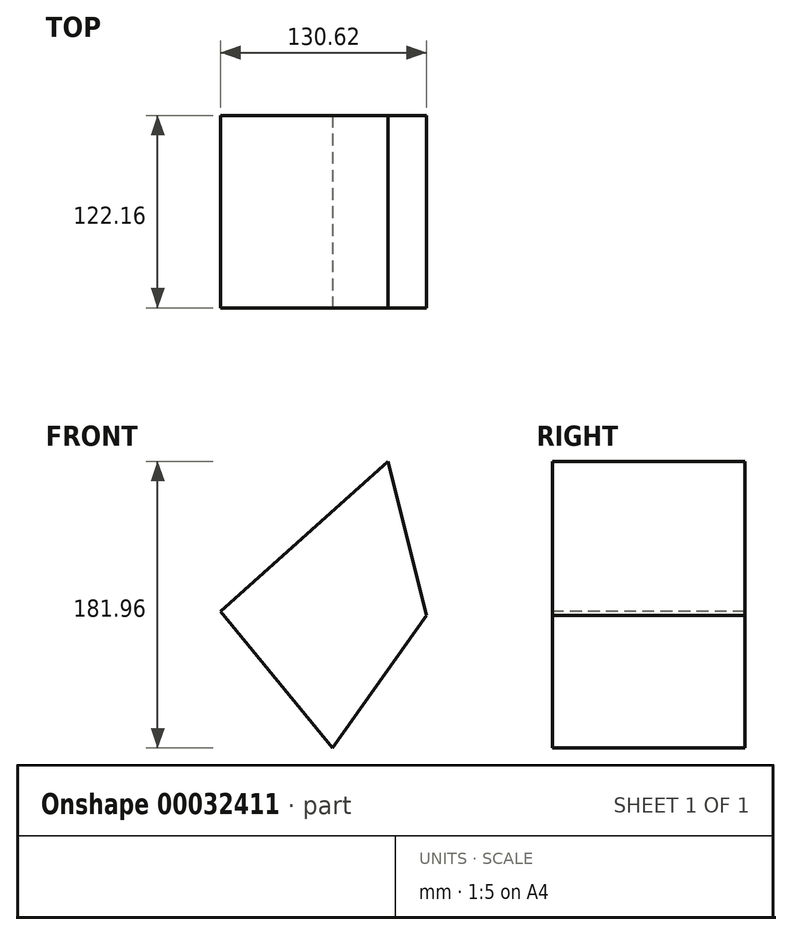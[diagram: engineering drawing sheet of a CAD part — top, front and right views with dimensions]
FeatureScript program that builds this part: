
annotation { "Feature Type Name" : "Feature", "Feature Type Description" : "" }
export const myFeature = defineFeature(function(context is Context, id is Id, definition is map)
    precondition{}
    {
        {
            var Q0;
            Q0=qCreatedBy(makeId("Front.planeOp"),FACE);
            var sketch = newSketch(context, id + "F0", { "sketchPlane" : qUnion([Q0])});
            skLineSegment(sketch, "E0", {"start": v(-81.06, 22.8) * mm, "end": v(25.2, 118.15) * mm});
            skLineSegment(sketch, "E1", {"start": v(25.2, 118.15) * mm, "end": v(49.56, 20.19) * mm});
            skLineSegment(sketch, "E2", {"start": v(49.56, 20.19) * mm, "end": v(-10.08, -63.8) * mm});
            skLineSegment(sketch, "E3", {"start": v(-10.08, -63.8) * mm, "end": v(-81.06, 22.8) * mm});
            skSolve(sketch);
        }
        {
            var Q0;
            Q0=makeQuery(id+"F0.imprint","IMPRINT",FACE,{"disambiguationData":[TD([[makeQuery(id+"F0.imprint","IMPRINT",EDGE,{"derivedFrom":sQuery(id+"F0.wireOp",EDGE,"E0")}),-1.0]])]});
            extrude(context, id + "F1", {"entities" : qUnion([Q0]), "oppositeDirection" : true, "depth" : 122.16 * mm});
        }
    });
